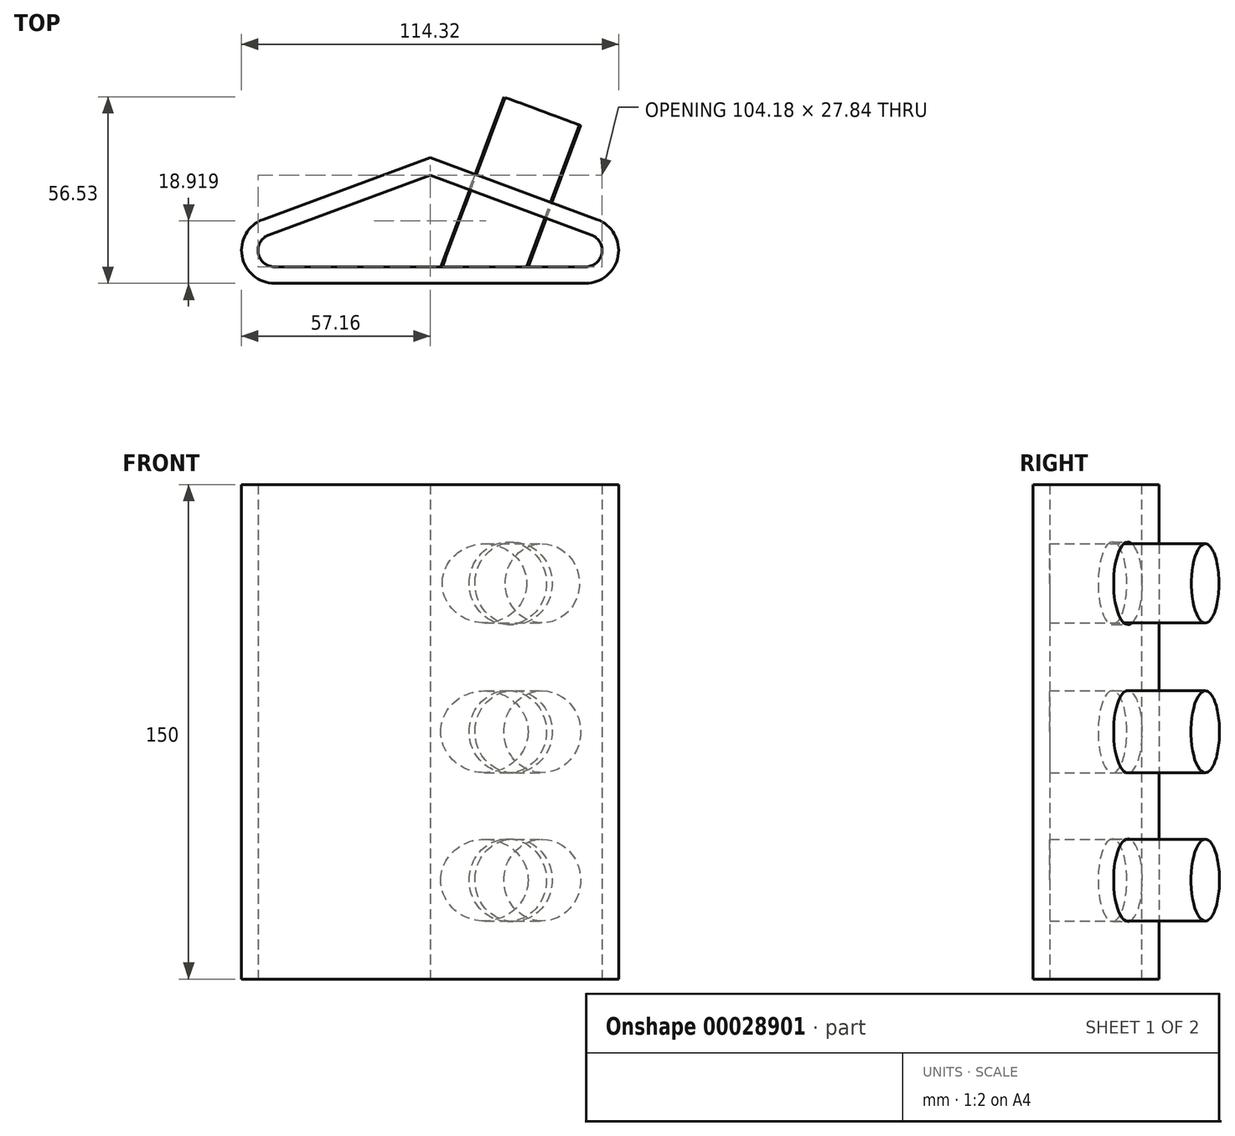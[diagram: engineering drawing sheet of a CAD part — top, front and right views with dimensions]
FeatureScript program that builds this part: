
annotation { "Feature Type Name" : "Feature", "Feature Type Description" : "" }
export const myFeature = defineFeature(function(context is Context, id is Id, definition is map)
    precondition{}
    {
        {
            var Q0;
            Q0=qCreatedBy(makeId("Top.planeOp"),FACE);
            var sketch = newSketch(context, id + "F0", { "sketchPlane" : qUnion([Q0])});
            skLineSegment(sketch, "E0", {"start": v(-48.9, 9.69) * mm, "end": v(0, 27.84) * mm});
            skLineSegment(sketch, "E1", {"start": v(0, 27.84) * mm, "end": v(48.9, 9.69) * mm});
            skLineSegment(sketch, "E2", {"start": v(-47.16, 0) * mm, "end": v(47.16, 0) * mm});
            skPoint(sketch, "E3.visualSharp", {"position": v(-75, 0) * mm});
            skArc(sketch, "E3.filletArc", {"start": v(-48.9, 9.69) * mm, "mid": v(-52.08, 4.12) * mm, "end": v(-47.16, 0) * mm});
            skPoint(sketch, "E4.visualSharp", {"position": v(75, 0) * mm});
            skArc(sketch, "E4.filletArc", {"start": v(47.16, 0) * mm, "mid": v(52.08, 4.12) * mm, "end": v(48.9, 9.69) * mm});
            skLineSegment(sketch, "E5.0", {"start": v(0, 33.17) * mm, "end": v(50.64, 14.37) * mm});
            skLineSegment(sketch, "E5.1", {"start": v(-50.64, 14.37) * mm, "end": v(0, 33.17) * mm});
            skArc(sketch, "E5.2", {"start": v(-50.64, 14.38) * mm, "mid": v(-57, 3.23) * mm, "end": v(-47.16, -5) * mm});
            skLineSegment(sketch, "E5.3", {"start": v(-47.16, -5) * mm, "end": v(47.16, -5) * mm});
            skArc(sketch, "E5.4", {"start": v(47.16, -5) * mm, "mid": v(57, 3.23) * mm, "end": v(50.64, 14.38) * mm});
            skSolve(sketch);
        }
        {
            var Q0;
            Q0=makeQuery(id+"F0.imprint","IMPRINT",FACE,{"disambiguationData":[TD([[makeQuery(id+"F0.imprint","IMPRINT",EDGE,{"derivedFrom":sQuery(id+"F0.wireOp",EDGE,"E0")}),1.0]])]});
            extrude(context, id + "F1", {"entities" : qUnion([Q0]), "depth" : 150 * mm});
        }
        {
            var Q0;
            Q0=makeQuery(id+"F1.opExtrude","SWEPT_FACE",FACE,{"disambiguationData":[OSD([sQuery(id+"F0.wireOp",EDGE,"E5.0")])]});
            var sketch = newSketch(context, id + "F2", { "sketchPlane" : qUnion([Q0])});
            skLineSegment(sketch, "E6", {"start": v(-15.47, 150) * mm, "end": v(-15.47, 0) * mm, "construction": true});
            skCircle(sketch, "E7", {"center": v(-15.47, 120) * mm, "radius": 12.5 * mm});
            skCircle(sketch, "E8", {"center": v(-15.47, 30) * mm, "radius": 12.5 * mm});
            skCircle(sketch, "E9", {"center": v(-15.47, 75) * mm, "radius": 12.5 * mm});
            skSolve(sketch);
        }
        {
            var Q0;
            Q0 = qSketchRegion(id + "F2", true);
            extrude(context, id + "F3", {"entities" : qUnion([Q0]), "operationType" : NewBodyOperationType.REMOVE, "endBound" : BoundingType.UP_TO_NEXT, "oppositeDirection" : true, "depth" : 14.78 * mm});
        }
        {
            var Q0;
            Q0=makeQuery(id+"F1.opExtrude","SWEPT_FACE",FACE,{"disambiguationData":[OSD([sQuery(id+"F0.wireOp",EDGE,"E5.0")])]});
            var sketch = newSketch(context, id + "F4", { "sketchPlane" : qUnion([Q0])});
            skCircle(sketch, "E10.0", {"center": v(-15.47, 120) * mm, "radius": 12 * mm});
            skSolve(sketch);
        }
        {
            var Q0;
            Q0=makeQuery(id+"F4.imprint","IMPRINT",FACE,{"disambiguationData":[TD([[makeQuery(id+"F4.imprint","IMPRINT",EDGE,{"derivedFrom":sQuery(id+"F4.wireOp",EDGE,"E10.0")}),1.0]])]});
            var Q1;
            Q1=makeQuery(id+"F1.opExtrude","SWEPT_FACE",FACE,{"disambiguationData":[OSD([sQuery(id+"F0.wireOp",EDGE,"E2")])]});
            extrude(context, id + "F5", {"entities" : qUnion([Q0]), "operationType" : NewBodyOperationType.ADD, "endBound" : BoundingType.UP_TO_SURFACE, "oppositeDirection" : true, "endBoundEntityFace" : qUnion([Q1]), "depth" : 25 * mm, "hasSecondDirection" : true, "secondDirectionOppositeDirection" : false, "secondDirectionDepth" : 25 * mm});
        }
        {
            var Q0;
            {var subQ0=sQuery(id+"F0.wireOp",EDGE,"E5.0");Q0=makeQuery(id+"F4.imprint","IMPRINT",FACE,{"disambiguationData":[TD([[makeQuery(id+"F4.imprint","IMPRINT",EDGE,{"derivedFrom":makeQuery(id+"F1.opExtrude","CAP_EDGE",EDGE,{"disambiguationData":[OSD([subQ0])],"isStart":true})}),-1.0]])]});}
            var sketch = newSketch(context, id + "F6", { "sketchPlane" : qUnion([Q0])});
            skCircle(sketch, "E11.0", {"center": v(-15.47, 75) * mm, "radius": 12.4 * mm});
            skSolve(sketch);
        }
        {
            var Q0;
            Q0 = qSketchRegion(id + "F6", true);
            var Q1;
            Q1=makeQuery(id+"F1.opExtrude","SWEPT_FACE",FACE,{"disambiguationData":[OSD([sQuery(id+"F0.wireOp",EDGE,"E2")])]});
            extrude(context, id + "F7", {"entities" : qUnion([Q0]), "operationType" : NewBodyOperationType.ADD, "endBound" : BoundingType.UP_TO_SURFACE, "oppositeDirection" : true, "endBoundEntityFace" : qUnion([Q1]), "depth" : 25 * mm, "hasSecondDirection" : true, "secondDirectionOppositeDirection" : false, "secondDirectionDepth" : 25 * mm});
        }
        {
            var Q0;
            {var subQ0=sQuery(id+"F0.wireOp",EDGE,"E5.0");Q0=makeQuery(id+"F4.imprint","IMPRINT",FACE,{"disambiguationData":[TD([[makeQuery(id+"F4.imprint","IMPRINT",EDGE,{"derivedFrom":makeQuery(id+"F1.opExtrude","CAP_EDGE",EDGE,{"disambiguationData":[OSD([subQ0])],"isStart":true})}),-1.0]])]});}
            var sketch = newSketch(context, id + "F8", { "sketchPlane" : qUnion([Q0])});
            skCircle(sketch, "E12.0", {"center": v(-15.47, 30) * mm, "radius": 12.4 * mm});
            skSolve(sketch);
        }
        {
            var Q0;
            Q0 = qSketchRegion(id + "F8", true);
            var Q1;
            Q1=makeQuery(id+"F1.opExtrude","SWEPT_FACE",FACE,{"disambiguationData":[OSD([sQuery(id+"F0.wireOp",EDGE,"E2")])]});
            extrude(context, id + "F9", {"entities" : qUnion([Q0]), "operationType" : NewBodyOperationType.ADD, "endBound" : BoundingType.UP_TO_SURFACE, "oppositeDirection" : true, "endBoundEntityFace" : qUnion([Q1]), "depth" : 23.83 * mm, "hasSecondDirection" : true, "secondDirectionOppositeDirection" : false, "secondDirectionDepth" : 25 * mm});
        }
    });
